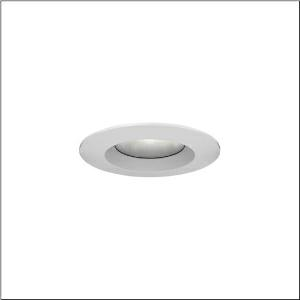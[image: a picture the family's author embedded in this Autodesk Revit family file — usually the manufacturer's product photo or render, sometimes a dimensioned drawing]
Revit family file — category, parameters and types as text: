
# Revit family: lunis_40_ip65_5dp10c72v365
name_source: partatom
category: Lighting Fixtures
units: mm (PartAtom-declared; Revit-internal decimal feet)

## family parameters
Cut with Voids When Loaded = No
Host = Face
Light Source = No
Part Type = Normal
Room Calculation Point = No
Round Connector Dimension = Use Diameter
Shared = No

## types (1)
- Lunis 40 IP65 (1 x LED, 350 lm, 3.5 W, 3000K)
    Apparent Load = 4 VA
    CIE Flux Codes = 57 88 99 100 100
    Color Rendering = 80
    Color Temperature = 3000K
    Default Elevation = 1800 mm
    Description = Lunis 40 IP65, downlight, of PMMA, light emission: direct distribution, LED rated luminous flux: 350lm, light colour: 830, control gear: ECG, mains connection: 220..240V, AC, 50/60Hz, housing, round, of aluminium, coated, traffic white (RAL 9016), diameter: 83mm, recess depth: 43mm, protection rating (complete): IP20, protection rating (on room side): IP65, insulation class (complete): insulation class II (safety insulation), certification: CE, permissible ambient temperature for indoor applications: -20..+40°C, packaging unit: 1 piece
    Height = 0 mm  [stored 0 ft]
    Lamp = 1 x LED
    Lamp Light Flux = 350 lm
    Lamp Power = 3.5 W
    Lamp count = 1
    Length = 83 mm
    Luminous efficacy = 100 lm/W
    Manufacturer = Siteco
    ModVariant = No
    Model = 5DP10C72V365
    Mounting Place = Ceiling
    Mounting Type = Recessed
    Number of Poles = 1
    OnlyDefault = Yes
    Power Factor = 1
    Product Name = Lunis 40 IP65
    Product group = downlight
    ProductGroupID = 400
    Protection Class = Protection class II
    Protection Degree = IP 20
    RLX_Detail_Level = 1
    RLX_Emergency_Light_Flux = 0 lm
    RLX_Emergency_Type = 0
    RLX_Emergency_Type_DB = No
    RlxData = <blob elided: 24093 chars, md5=dc404e76>
    Socket = socket
    Standby Power = 0 W
    System Light Flux = 350 lm
    System Power = 4 W
    Type Comments = Product without accessories
    Type Image = l_1006628.jpg
    URL = http://relux.com
    VarID = ---
    Voltage = 0 V
    Weight = 0.00 kg
    Width = 0 mm  [stored 0 ft]

note: [stored X ft] marks values corroborated as IEEE doubles in the binary element streams (Revit-internal decimal feet)

## geometry (parser evidence)
native form markers: Blend x4, Sweep x10
no freeform markers — native parametric forms only
